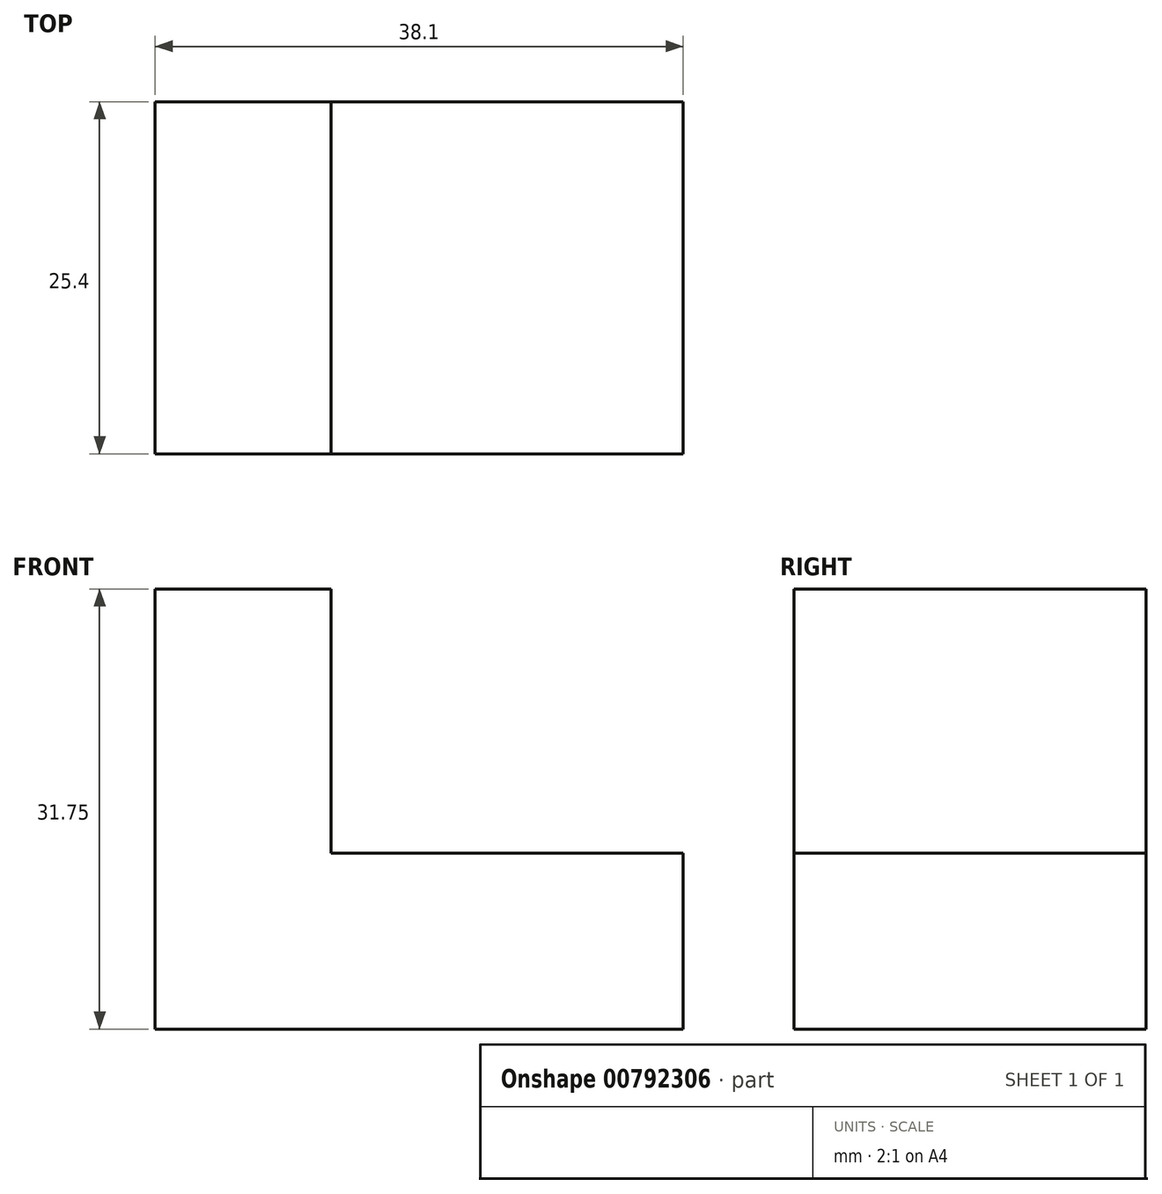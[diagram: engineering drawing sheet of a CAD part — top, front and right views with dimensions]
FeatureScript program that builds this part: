
annotation { "Feature Type Name" : "Feature", "Feature Type Description" : "" }
export const myFeature = defineFeature(function(context is Context, id is Id, definition is map)
    precondition{}
    {
        {
            var Q0;
            Q0=qCreatedBy(makeId("Front.planeOp"),FACE);
            var sketch = newSketch(context, id + "F0", { "sketchPlane" : qUnion([Q0])});
            skLineSegment(sketch, "E0", {"start": v(0, 31.75) * mm, "end": v(0, 0) * mm});
            skLineSegment(sketch, "E1", {"start": v(0, 0) * mm, "end": v(38.1, 0) * mm});
            skLineSegment(sketch, "E2", {"start": v(38.1, 0) * mm, "end": v(38.1, 12.7) * mm});
            skLineSegment(sketch, "E3", {"start": v(38.1, 12.7) * mm, "end": v(12.7, 12.7) * mm});
            skLineSegment(sketch, "E4", {"start": v(12.7, 12.7) * mm, "end": v(12.7, 31.75) * mm});
            skLineSegment(sketch, "E5", {"start": v(12.7, 31.75) * mm, "end": v(0, 31.75) * mm});
            skSolve(sketch);
        }
        {
            var Q0;
            Q0=qSketchRegion(id+"F0",true);
            extrude(context, id + "F1", {"entities" : qUnion([Q0]), "depth" : 25.4 * mm, "offsetDistance" : 25.4 * mm});
        }
    });
